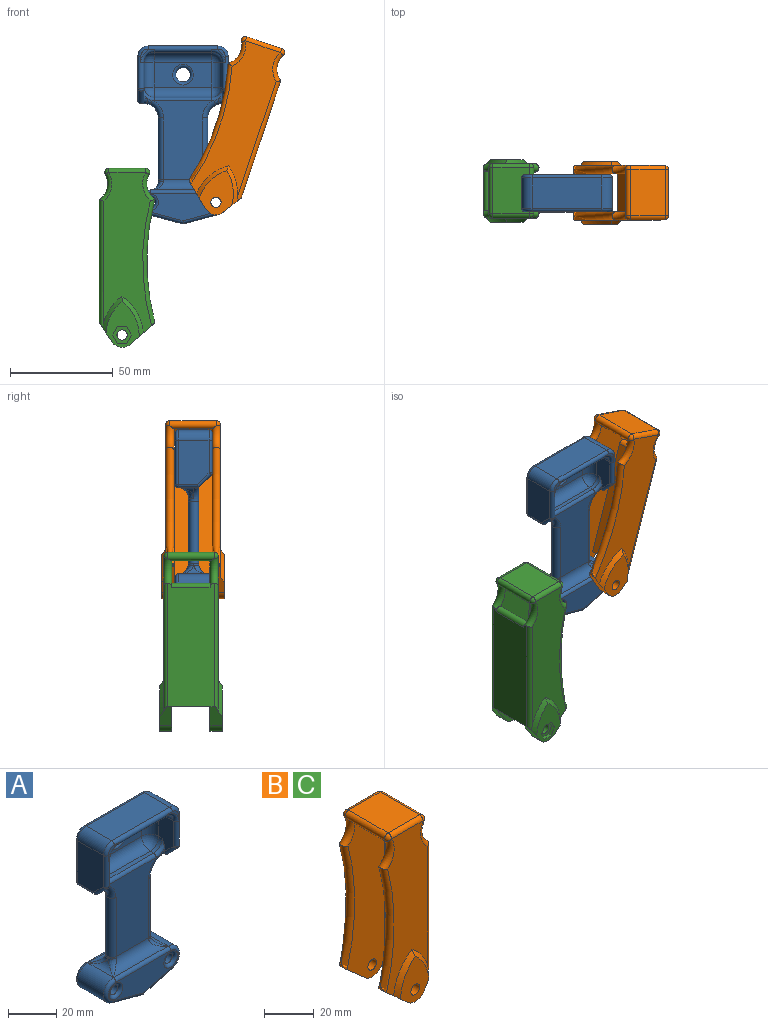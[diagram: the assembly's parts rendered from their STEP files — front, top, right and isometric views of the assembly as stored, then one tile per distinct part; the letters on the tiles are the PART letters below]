
ASSEMBLY  parts=3 mates=1
PART A: 108 faces, bbox 45.4x18.4x87.3 mm
  f0: cylinder r=2.5mm len=2.05mm, axis (-1,0,0), area 0mm2, adj f1,f107
  f1: cylinder r=1.5mm len=8.56mm, axis (0,-0.71,0.71), area 40mm2, adj f0,f2,f102,f103,f104,f105,f106
  f2: sphere r=1.5mm, area 3.5mm2, adj f1,f3
  f3: cylinder r=1.5mm len=15.88mm, axis (0,0,1), area 67.8mm2, adj f2,f4,f100,f101,f102,f106
  f4: torus R=3.5mm, axis (0,-1,0), area 16.5mm2, adj f3,f5,f99,f100
  f5: cylinder r=5mm len=15mm, axis (0,-1,0), area 117.8mm2, adj f4,f6,f98,f106
  f6: torus R=3.5mm, axis (0,-1,0), area 16.5mm2, adj f5,f7,f96,f97
  f7: cylinder r=1.5mm len=21.5mm, axis (0,0,-1), area 50.7mm2, adj f6,f8,f96,f106
  f8: sphere r=1.5mm, area 3.5mm2, adj f7,f9,f105
  f9: cylinder r=1.5mm len=41mm, axis (1,0,0), area 96.6mm2, adj f8,f10,f94,f95,f96,f104
  f10: plane 7.5x1.5mm, normal (0,0,-1), area 11.3mm2, adj f9,f11,f92,f93
  f11: cylinder r=7mm len=7.5mm, axis (0,1,0), area 26.4mm2, adj f10,f12,f89,f90,f91
  f12: torus R=9.5mm, axis (0,-1,0), area 41.4mm2, adj f11,f13,f87,f88,f89,f91
  f13: plane 32x19.43mm, normal (0,1,0), area 608.3mm2, adj f12,f14,f50,f86,f87,f95
  f14: cylinder r=5mm len=32mm, axis (1,0,0), area 183.6mm2, adj f13,f15,f46,f47,f48,f49
  f15: cylinder r=1.5mm len=32mm, axis (-1,0,0), area 75.4mm2, adj f14,f16,f44,f45
  f16: plane 41x13.45mm, normal (0,1,0), area 324.9mm2, adj f15,f17,f41,f42,f43,f44,f45
  f17: torus R=4mm, axis (0,-1,0), area 45.1mm2, adj f16,f18
  f18: cylinder r=2.5mm len=15mm, axis (0,1,0), area 235.6mm2, adj f17,f19
  f19: torus R=4mm, axis (0,-1,0), area 45.1mm2, adj f18,f20
  f20: plane 41x13.45mm, normal (0,-1,0), area 324.9mm2, adj f19,f21,f35,f36,f37,f38,f39
  f21: cylinder r=1.5mm len=32mm, axis (1,0,0), area 75.4mm2, adj f20,f22,f35,f38
  f22: cylinder r=5mm len=32mm, axis (-1,0,0), area 183.6mm2, adj f21,f23,f32,f33,f34,f88
  f23: torus R=7.5mm, axis (1,0,0), area 3.1mm2, adj f22,f24,f32,f86
  f24: plane 1x0.13mm, normal (-1,0,0), area 0mm2, adj f23,f25,f47
  f25: cylinder r=4mm len=15mm, axis (0,1,0), area 37mm2, adj f24,f26,f32,f46
  f26: cylinder r=6mm len=15mm, axis (0,1,0), area 259.2mm2, adj f25,f27,f38,f45
  f27: plane 17.55x15mm, normal (-0.26,0,-0.97), area 272.6mm2, adj f26,f28,f37,f41
  f28: plane 17.55x15mm, normal (0.26,0,-0.97), area 272.6mm2, adj f27,f29,f36,f42
  f29: cylinder r=6mm len=15mm, axis (0,1,0), area 259.2mm2, adj f28,f30,f35,f44
  f30: cylinder r=4mm len=15mm, axis (0,-1,0), area 37mm2, adj f29,f31,f33,f49
  f31: plane 1x0.13mm, normal (1,0,0), area 0mm2, adj f30,f34,f48
  f32: bspline ~7.5x6.5mm, area 19.4mm2, adj f22,f23,f25
  f33: bspline ~7.5x6.5mm, area 19.4mm2, adj f22,f30,f34
  f34: torus R=7.5mm, axis (1,0,0), area 3.1mm2, adj f22,f31,f33,f87
  f35: torus R=4.5mm, axis (0,-1,0), area 37mm2, adj f20,f21,f29,f36
  f36: cylinder r=1.5mm len=17.94mm, axis (-0.97,0,-0.26), area 42.3mm2, adj f20,f28,f35,f37
  f37: cylinder r=1.5mm len=17.94mm, axis (-0.97,0,0.26), area 42.3mm2, adj f20,f27,f36,f38
  f38: torus R=4.5mm, axis (0,-1,0), area 37mm2, adj f20,f21,f26,f37
  f39: torus R=4mm, axis (0,-1,0), area 45.1mm2, adj f20,f40
  f40: cylinder r=2.5mm len=15mm, axis (0,1,0), area 235.6mm2, adj f39,f43
  f41: cylinder r=1.5mm len=17.94mm, axis (0.97,0,-0.26), area 42.3mm2, adj f16,f27,f42,f45
  f42: cylinder r=1.5mm len=17.94mm, axis (0.97,0,0.26), area 42.3mm2, adj f16,f28,f41,f44
  f43: torus R=4mm, axis (0,-1,0), area 45.1mm2, adj f16,f40
  f44: torus R=4.5mm, axis (0,-1,0), area 37mm2, adj f15,f16,f29,f42
  f45: torus R=4.5mm, axis (0,-1,0), area 37mm2, adj f15,f16,f26,f41
  f46: bspline ~7.5x6.5mm, area 19.4mm2, adj f14,f25,f47
  f47: torus R=7.5mm, axis (1,0,0), area 3.1mm2, adj f14,f24,f46,f86
  f48: torus R=7.5mm, axis (1,0,0), area 3.1mm2, adj f14,f31,f49,f87
  f49: bspline ~7.5x6.5mm, area 19.4mm2, adj f14,f30,f48
  f50: torus R=9.5mm, axis (0,-1,0), area 41.4mm2, adj f13,f51,f52,f53,f86,f88
  f51: bspline ~9.49x7.5mm, area 24.7mm2, adj f50,f52,f95
  f52: cylinder r=7mm len=7.5mm, axis (0,-1,0), area 26.4mm2, adj f50,f51,f53,f104,f107
  f53: bspline ~4.02x3.63mm, area 7.6mm2, adj f50,f52,f54,f107
  f54: torus R=6.5mm, axis (0,-1,0), area 15.8mm2, adj f53,f55,f84,f85,f88,f102
  f55: cylinder r=5mm len=5mm, axis (0,-1,0), area 15.7mm2, adj f54,f56,f83,f102
  f56: plane 28x2mm, normal (0,0,1), area 56mm2, adj f55,f57,f82,f84
  f57: cylinder r=5mm len=28mm, axis (1,0,0), area 219.9mm2, adj f56,f58,f80,f83
  f58: sphere r=5mm, area 39.3mm2, adj f57,f59,f82
  f59: cylinder r=5mm len=12mm, axis (0,0,1), area 94.2mm2, adj f58,f60,f77,f80
  f60: sphere r=5mm, area 39.3mm2, adj f59,f61,f66
  f61: cylinder r=5mm len=28mm, axis (-1,0,0), area 219.9mm2, adj f60,f62,f65,f80
  f62: sphere r=5mm, area 39.3mm2, adj f61,f63,f64
  f63: cylinder r=5mm len=8.5mm, axis (0,-1,0), area 66.8mm2, adj f62,f65,f101,f102
  f64: cylinder r=5mm len=12mm, axis (0,0,-1), area 94.2mm2, adj f62,f80,f83,f102
  f65: plane 28x8.5mm, normal (0,0,-1), area 238mm2, adj f61,f63,f66,f99
  f66: cylinder r=5mm len=8.5mm, axis (0,1,0), area 66.8mm2, adj f60,f65,f67,f77
  f67: torus R=6.5mm, axis (0,-1,0), area 20.5mm2, adj f66,f68,f76,f99
  f68: plane 6.5x6.5mm, normal (0,-1,0), area 6.4mm2, adj f67,f69,f76,f99
  f69: torus R=3.5mm, axis (0,-1,0), area 16.5mm2, adj f68,f70,f76,f99
  f70: cylinder r=5mm len=15mm, axis (0,1,0), area 117.8mm2, adj f69,f71,f73,f98
  f71: torus R=3.5mm, axis (0,-1,0), area 16.5mm2, adj f70,f72,f96,f97
  f72: cylinder r=1.5mm len=21.5mm, axis (0,0,1), area 50.7mm2, adj f71,f73,f94,f96
  f73: plane 21.5x15mm, normal (1,0,0), area 306.7mm2, adj f70,f72,f74,f76,f93
  f74: cylinder r=1.5mm len=7.12mm, axis (0,-0.71,0.71), area 39.1mm2, adj f73,f75,f77,f92,f93
  f75: sphere r=1.5mm, area 3.5mm2, adj f74,f76
  f76: cylinder r=1.5mm len=15.88mm, axis (0,0,-1), area 67.8mm2, adj f67,f68,f69,f73,f75,f77
  f77: plane 18.32x8.9mm, normal (-1,0,0), area 121.2mm2, adj f59,f66,f74,f76,f78,f79,f82,f90
  f78: torus R=6.5mm, axis (0,-1,0), area 15.8mm2, adj f77,f79,f82,f84,f88,f91
  f79: plane 1.84x1.53mm, normal (0,-1,0), area 1mm2, adj f77,f78,f90
  f80: plane 28x12mm, normal (0,-1,0), area 257.5mm2, adj f57,f59,f61,f64,f81
  f81: torus R=5mm, axis (0,-1,0), area 119.8mm2, adj f80,f96
  f82: cylinder r=5mm len=5mm, axis (0,1,0), area 15.7mm2, adj f56,f58,f77,f78
  f83: sphere r=5mm, area 39.3mm2, adj f55,f57,f64
  f84: cylinder r=1.5mm len=28mm, axis (1,0,0), area 66mm2, adj f54,f56,f78,f88
  f85: plane 1.84x1.53mm, normal (0,-1,0), area 1mm2, adj f54,f102,f107
  f86: cylinder r=2.5mm len=30mm, axis (0,0,-1), area 235.6mm2, adj f13,f23,f47,f50,f88
  f87: cylinder r=2.5mm len=30mm, axis (0,0,-1), area 235.6mm2, adj f12,f13,f34,f48,f88
  f88: plane 38.56x29.76mm, normal (0,-1,0), area 757mm2, adj f12,f22,f50,f54,f78,f84,f86,f87
  f89: bspline ~9.49x7.5mm, area 24.7mm2, adj f11,f12,f95
  f90: torus R=9.5mm, axis (0,-1,0), area 6.1mm2, adj f11,f77,f79,f91,f92
  f91: bspline ~3.99x3.65mm, area 7.6mm2, adj f11,f12,f78,f90
  f92: cylinder r=2.5mm len=2.47mm, axis (-1,0,0), area 1.9mm2, adj f10,f74,f90,f93
  f93: cylinder r=1.5mm len=10mm, axis (0,1,0), area 25.6mm2, adj f10,f73,f74,f92,f94
  f94: sphere r=1.5mm, area 3.5mm2, adj f9,f72,f93
  f95: cylinder r=5mm len=38mm, axis (-1,0,0), area 210.7mm2, adj f9,f13,f51,f89
  f96: plane 41x25mm, normal (0,1,0), area 941.2mm2, adj f6,f7,f9,f71,f72,f81,f97
  f97: cylinder r=1.5mm len=34mm, axis (-1,0,0), area 80.1mm2, adj f6,f71,f96,f98
  f98: plane 34x15mm, normal (0,0,1), area 510mm2, adj f5,f70,f97,f99
  f99: cylinder r=1.5mm len=34mm, axis (1,0,0), area 146.1mm2, adj f4,f65,f67,f68,f69,f98,f100,f101
  f100: plane 6.5x6.5mm, normal (0,-1,0), area 6.4mm2, adj f3,f4,f99,f101
  f101: torus R=6.5mm, axis (0,-1,0), area 20.5mm2, adj f3,f63,f99,f100
  f102: plane 18.32x8.9mm, normal (1,0,0), area 121.2mm2, adj f1,f3,f54,f55,f63,f64,f85,f107
  f103: cylinder r=2.5mm len=0.41mm, axis (-1,0,0), area 0mm2, adj f1,f104,f107
  f104: plane 10x1.5mm, normal (0,0,-1), area 14.3mm2, adj f1,f9,f52,f103,f105
  f105: cylinder r=1.5mm len=10mm, axis (0,-1,0), area 22.8mm2, adj f1,f8,f104,f106
  f106: plane 21.5x15mm, normal (-1,0,0), area 306.7mm2, adj f1,f3,f5,f7,f105
  f107: torus R=9.5mm, axis (0,-1,0), area 6.1mm2, adj f0,f52,f53,f85,f102,f103
PART B: 49 faces, bbox 28.2x30.7x87.2 mm
  f0: plane 78.02x23.33mm, normal (0,1,0), area 1299.3mm2, adj f1,f26,f27,f30,f31,f37,f38,f40
  f1: plane 11.21x9.79mm, normal (-0.66,0,-0.75), area 73.1mm2, adj f0,f2,f15,f25,f26,f36,f37
  f2: cylinder r=6mm len=8.99mm, axis (0,1,0), area 61.8mm2, adj f1,f3,f15,f25
  f3: plane 9.41x6.17mm, normal (0.84,0,-0.54), area 55.8mm2, adj f2,f9,f15,f25,f27,f30
  f4: cylinder r=2.5mm len=5mm, axis (0,1,0), area 62.8mm2, adj f12,f15
  f5: plane 22.5x17.94mm, normal (0,0,1), area 403.6mm2, adj f32,f38,f42,f43
  f6: plane 11.21x9.79mm, normal (-0.66,0,-0.75), area 73.1mm2, adj f7,f11,f14,f18,f28,f46,f47
  f7: cylinder r=6mm len=8.99mm, axis (0,1,0), area 61.8mm2, adj f6,f8,f14,f18
  f8: plane 9.41x6.17mm, normal (0.84,0,-0.54), area 55.8mm2, adj f7,f9,f14,f18,f29,f33
  f9: plane 60x22.5mm, normal (1,0,0), area 1311mm2, adj f3,f8,f13,f30,f31,f33,f35,f48
  f10: cylinder r=2.5mm len=6mm, axis (0,1,0), area 94.2mm2, adj f14,f18
  f11: plane 78.02x23.33mm, normal (0,-1,0), area 1299.3mm2, adj f6,f28,f29,f33,f35,f42,f45,f46
  f12: plane 9.06x7.85mm, normal (0,1,0), area 33.7mm2, adj f4,f19,f20,f21,f22,f23,f24
  f13: plane 18.5x4mm, normal (0,0,-1), area 74mm2, adj f9,f14,f15,f17
  f14: plane 83x25.33mm, normal (0,1,0), area 1450.3mm2, adj f6,f7,f8,f10,f13,f16,f17,f35
  f15: plane 83x25.33mm, normal (0,-1,0), area 1450.3mm2, adj f1,f2,f3,f4,f13,f16,f17,f31
  f16: plane 18.88x17.94mm, normal (0,0,-1), area 332.1mm2, adj f14,f15,f31,f32,f35,f40,f43,f45
  f17: plane 58x18.5mm, normal (-1,0,0), area 1073mm2, adj f13,f14,f15,f48
  f18: plane 22.29x16.06mm, normal (0,-1,0), area 224.4mm2, adj f6,f7,f8,f10,f28,f29
  f19: plane 3.93x2.27mm, normal (0.87,0,0.5), area 9.1mm2, adj f12,f20,f24,f25
  f20: plane 4.53x2mm, normal (0,0,1), area 9.1mm2, adj f12,f19,f21,f25
  f21: plane 3.93x2.27mm, normal (-0.87,0,0.5), area 9.1mm2, adj f12,f20,f22,f25
  f22: plane 3.93x2.27mm, normal (-0.87,0,-0.5), area 9.1mm2, adj f12,f21,f23,f25
  f23: plane 4.53x2mm, normal (0,0,-1), area 9.1mm2, adj f12,f22,f24,f25
  f24: plane 3.93x2.27mm, normal (0.87,0,-0.5), area 9.1mm2, adj f12,f19,f23,f25
  f25: plane 22.29x16.06mm, normal (0,1,0), area 190.7mm2, adj f1,f2,f3,f19,f20,f21,f22,f23
  f26: cone r=20mm half-angle=45deg, axis (0,-1,0), area 57.9mm2, adj f0,f1,f25,f27
  f27: cone r=20mm half-angle=45deg, axis (0,-1,0), area 51.1mm2, adj f0,f3,f25,f26,f30
  f28: cone r=20mm half-angle=45deg, axis (0,1,0), area 57.9mm2, adj f6,f11,f18,f29
  f29: cone r=20mm half-angle=45deg, axis (0,1,0), area 51.1mm2, adj f8,f11,f18,f28,f33
  f30: cylinder r=2mm len=62.24mm, axis (0,0,1), area 190mm2, adj f0,f3,f9,f27,f31
  f31: torus R=11.03mm, axis (0,-1,0), area 85.3mm2, adj f0,f9,f15,f16,f30,f32,f34,f48
  f32: cylinder r=2mm len=22.5mm, axis (0,1,0), area 137.1mm2, adj f5,f16,f31,f34,f35,f39
  f33: cylinder r=2mm len=62.24mm, axis (0,0,-1), area 190mm2, adj f8,f9,f11,f29,f35
  f34: sphere r=2mm, area 8.4mm2, adj f31,f32,f38
  f35: torus R=11.03mm, axis (0,-1,0), area 85.3mm2, adj f9,f11,f14,f16,f32,f33,f39,f48
  f36: cylinder r=2mm len=3.59mm, axis (0,1,0), area 4.5mm2, adj f1,f37
  f37: torus R=116.5mm, axis (0,-1,0), area 381mm2, adj f0,f1,f15,f36,f40
  f38: cylinder r=2mm len=17.94mm, axis (-1,0,0), area 56.4mm2, adj f0,f5,f34,f41
  f39: sphere r=2mm, area 8.4mm2, adj f32,f35,f42
  f40: torus R=11.03mm, axis (0,-1,0), area 84.9mm2, adj f0,f15,f16,f37,f41,f43
  f41: sphere r=2mm, area 8.4mm2, adj f38,f40,f43
  f42: cylinder r=2mm len=17.94mm, axis (1,0,0), area 56.4mm2, adj f5,f11,f39,f44
  f43: cylinder r=2mm len=22.5mm, axis (0,1,0), area 137.1mm2, adj f5,f16,f40,f41,f44,f45
  f44: sphere r=2mm, area 8.4mm2, adj f42,f43,f45
  f45: torus R=11.03mm, axis (0,-1,0), area 84.9mm2, adj f11,f14,f16,f43,f44,f46
  f46: torus R=116.5mm, axis (0,-1,0), area 381mm2, adj f6,f11,f14,f45,f47
  f47: cylinder r=2mm len=3.59mm, axis (0,1,0), area 4.5mm2, adj f6,f46
  f48: cylinder r=2mm len=19.32mm, axis (0,1,0), area 118mm2, adj f9,f14,f15,f17,f31,f35
PART C: same geometry as B
PLACE A t=(95.61,-37.59,1.7)mm fixed
PLACE B rot(axis=(0,1,0),18.6deg) t=(118.84,-24.09,3.83)mm
PLACE C rot(axis=(0,0,-1),180deg) t=(71,-49.55,-60.3)mm
MATE revolute B.f2 <-> A.f29  axis (0,1,0) through (111.61,-46.59,-33.3)mm
